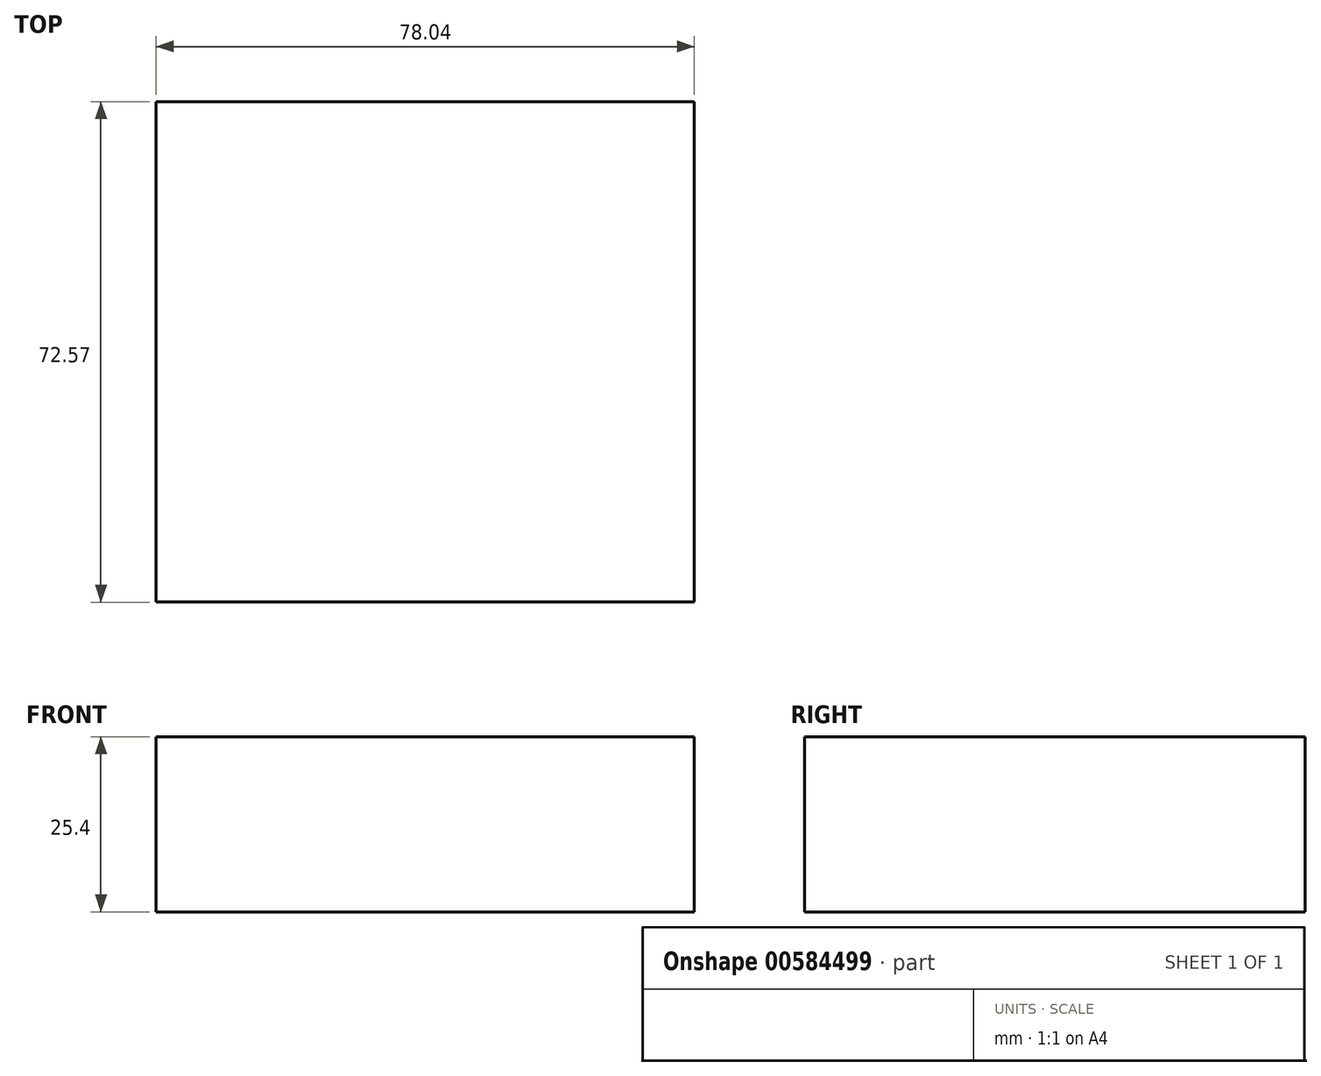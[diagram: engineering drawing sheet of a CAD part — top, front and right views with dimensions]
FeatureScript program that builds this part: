
annotation { "Feature Type Name" : "Feature", "Feature Type Description" : "" }
export const myFeature = defineFeature(function(context is Context, id is Id, definition is map)
    precondition{}
    {
        {
            var Q0;
            Q0=qCreatedBy(makeId("Top.planeOp"),FACE);
            var sketch = newSketch(context, id + "F0", { "sketchPlane" : qUnion([Q0])});
            skLineSegment(sketch, "E0.bottom", {"start": v(0, 0) * mm, "end": v(78.04, 0) * mm});
            skLineSegment(sketch, "E0.top", {"start": v(0, -72.57) * mm, "end": v(78.04, -72.57) * mm});
            skLineSegment(sketch, "E0.left", {"start": v(0, 0) * mm, "end": v(0, -72.57) * mm});
            skLineSegment(sketch, "E0.right", {"start": v(78.04, 0) * mm, "end": v(78.04, -72.57) * mm});
            skSolve(sketch);
        }
        {
            var Q0;
            Q0 = qSketchRegion(id + "F0", true);
            extrude(context, id + "F1", {"entities" : qUnion([Q0]), "depth" : 25.4 * mm, "offsetDistance" : 25.4 * mm});
        }
    });
